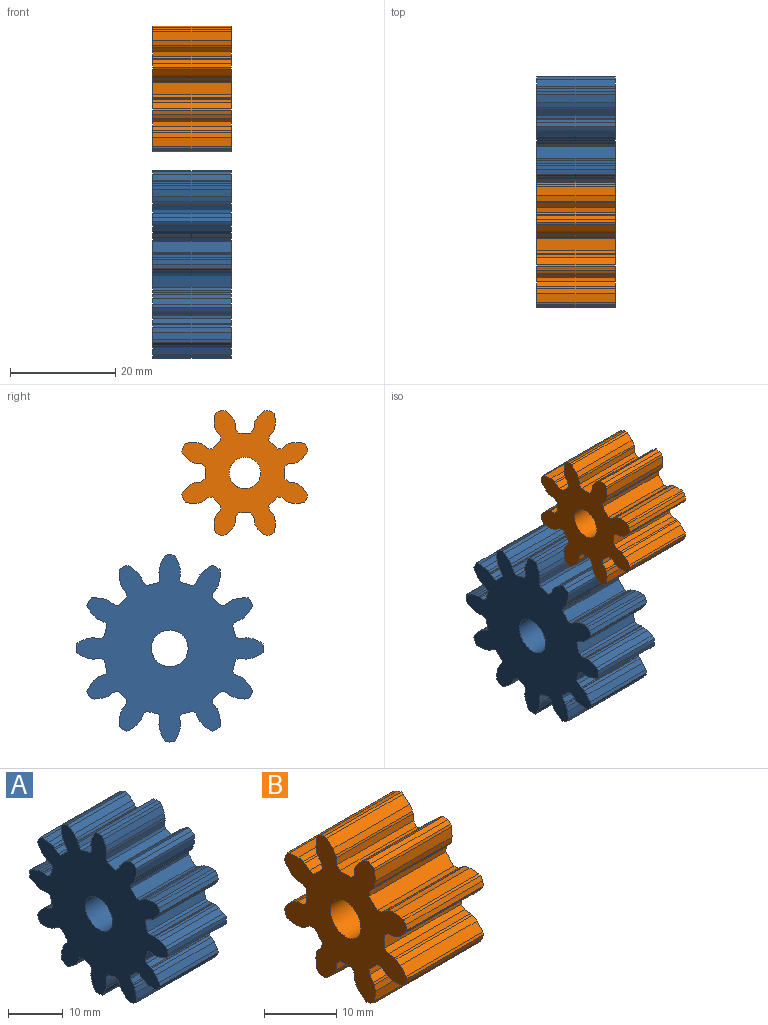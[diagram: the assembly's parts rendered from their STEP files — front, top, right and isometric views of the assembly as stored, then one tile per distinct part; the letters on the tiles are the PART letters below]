
ASSEMBLY  parts=2 mates=1
PART A: 231 faces, bbox 15x35.7x35.7 mm
  f0: plane 15x1.4mm, normal (0,-0.11,-0.99), area 21.2mm2, adj f1,f227,f228,f229
  f1: plane 15x0.66mm, normal (0,0.07,-1), area 10mm2, adj f0,f2,f228,f229
  f2: plane 15x0.69mm, normal (0,0.82,-0.57), area 12.7mm2, adj f1,f3,f228,f229
  f3: plane 15x0.77mm, normal (0,0.91,-0.42), area 12.7mm2, adj f2,f4,f228,f229
  f4: plane 15x0.6mm, normal (0,0.9,0.44), area 10mm2, adj f3,f5,f228,f229
  f5: plane 15x1.14mm, normal (0,0.81,0.59), area 21.2mm2, adj f4,f6,f228,f229
  f6: plane 15x0.7mm, normal (0,0.69,0.72), area 14.6mm2, adj f5,f7,f228,f229
  f7: plane 15x0.44mm, normal (0,0.56,0.83), area 7.9mm2, adj f6,f8,f228,f229
  f8: plane 15x0.08mm, normal (0,0.4,0.91), area 1.3mm2, adj f7,f9,f228,f229
  f9: plane 15x0.25mm, normal (0,0.24,0.97), area 3.9mm2, adj f8,f10,f228,f229
  f10: plane 15x0.9mm, normal (0,0.45,0.9), area 15mm2, adj f9,f11,f228,f229
  f11: plane 15x0.51mm, normal (0,0.83,0.56), area 9.3mm2, adj f10,f12,f228,f229
  f12: plane 15x2.2mm, normal (0,0.97,-0.26), area 34.2mm2, adj f11,f13,f228,f229
  f13: plane 15x0.56mm, normal (0,0.44,-0.9), area 9.3mm2, adj f12,f14,f228,f229
  f14: plane 15x1mm, normal (0,-0.06,-1), area 15mm2, adj f13,f15,f228,f229
  f15: plane 15x0.25mm, normal (0,-0.28,-0.96), area 3.9mm2, adj f14,f16,f228,f229
  f16: plane 15x0.09mm, normal (0,-0.11,-0.99), area 1.3mm2, adj f15,f17,f228,f229
  f17: plane 15x0.53mm, normal (0,0.07,-1), area 7.9mm2, adj f16,f18,f228,f229
  f18: plane 15x0.94mm, normal (0,0.24,-0.97), area 14.6mm2, adj f17,f19,f228,f229
  f19: plane 15x1.29mm, normal (0,0.4,-0.91), area 21.2mm2, adj f18,f20,f228,f229
  f20: plane 15x0.55mm, normal (0,0.56,-0.83), area 10mm2, adj f19,f21,f228,f229
  f21: plane 15x0.84mm, normal (0,1,-0.09), area 12.7mm2, adj f20,f22,f228,f229
  f22: plane 15x0.84mm, normal (0,1,0.09), area 12.7mm2, adj f21,f23,f228,f229
  f23: plane 15x0.55mm, normal (0,0.56,0.83), area 10mm2, adj f22,f24,f228,f229
  f24: plane 15x1.29mm, normal (0,0.4,0.91), area 21.2mm2, adj f23,f25,f228,f229
  f25: plane 15x0.94mm, normal (0,0.24,0.97), area 14.6mm2, adj f24,f26,f228,f229
  f26: plane 15x0.53mm, normal (0,0.07,1), area 7.9mm2, adj f25,f27,f228,f229
  f27: plane 15x0.09mm, normal (0,-0.11,0.99), area 1.3mm2, adj f26,f28,f228,f229
  f28: plane 15x0.25mm, normal (0,-0.28,0.96), area 3.9mm2, adj f27,f29,f228,f229
  f29: plane 15x1mm, normal (0,-0.06,1), area 15mm2, adj f28,f30,f228,f229
  f30: plane 15x0.56mm, normal (0,0.44,0.9), area 9.3mm2, adj f29,f31,f228,f229
  f31: plane 15x2.2mm, normal (0,0.97,0.26), area 34.2mm2, adj f30,f32,f228,f229
  f32: plane 15x0.51mm, normal (0,0.83,-0.56), area 9.3mm2, adj f31,f33,f228,f229
  f33: plane 15x0.9mm, normal (0,0.45,-0.9), area 15mm2, adj f32,f34,f228,f229
  f34: plane 15x0.25mm, normal (0,0.24,-0.97), area 3.9mm2, adj f33,f35,f228,f229
  f35: plane 15x0.08mm, normal (0,0.4,-0.91), area 1.3mm2, adj f34,f36,f228,f229
  f36: plane 15x0.44mm, normal (0,0.56,-0.83), area 7.9mm2, adj f35,f37,f228,f229
  f37: plane 15x0.7mm, normal (0,0.69,-0.72), area 14.6mm2, adj f36,f38,f228,f229
  f38: plane 15x1.14mm, normal (0,0.81,-0.59), area 21.2mm2, adj f37,f39,f228,f229
  f39: plane 15x0.6mm, normal (0,0.9,-0.44), area 10mm2, adj f38,f40,f228,f229
  f40: plane 15x0.77mm, normal (0,0.91,0.42), area 12.7mm2, adj f39,f41,f228,f229
  f41: plane 15x0.69mm, normal (0,0.82,0.57), area 12.7mm2, adj f40,f42,f228,f229
  f42: plane 15x0.66mm, normal (0,0.07,1), area 10mm2, adj f41,f43,f228,f229
  f43: plane 15x1.4mm, normal (0,-0.11,0.99), area 21.2mm2, adj f42,f44,f228,f229
  f44: plane 15x0.93mm, normal (0,-0.28,0.96), area 14.6mm2, adj f43,f45,f228,f229
  f45: plane 15x0.48mm, normal (0,-0.44,0.9), area 7.9mm2, adj f44,f46,f228,f229
  f46: plane 15x0.07mm, normal (0,-0.59,0.81), area 1.3mm2, adj f45,f47,f228,f229
  f47: plane 15x0.19mm, normal (0,-0.72,0.69), area 3.9mm2, adj f46,f48,f228,f229
  f48: plane 15x0.83mm, normal (0,-0.55,0.83), area 15mm2, adj f47,f49,f228,f229
  f49: plane 15x0.62mm, normal (0,-0.07,1), area 9.3mm2, adj f48,f50,f228,f229
  f50: plane 15x1.61mm, normal (0,0.71,0.71), area 34.2mm2, adj f49,f51,f228,f229
  f51: plane 15x0.62mm, normal (0,1,-0.07), area 9.3mm2, adj f50,f52,f228,f229
  f52: plane 15x0.83mm, normal (0,0.83,-0.55), area 15mm2, adj f51,f53,f228,f229
  f53: plane 15x0.19mm, normal (0,0.69,-0.72), area 3.9mm2, adj f52,f54,f228,f229
  f54: plane 15x0.07mm, normal (0,0.81,-0.59), area 1.3mm2, adj f53,f55,f228,f229
  f55: plane 15x0.48mm, normal (0,0.9,-0.44), area 7.9mm2, adj f54,f56,f228,f229
  f56: plane 15x0.93mm, normal (0,0.96,-0.28), area 14.6mm2, adj f55,f57,f228,f229
  f57: plane 15x1.4mm, normal (0,0.99,-0.11), area 21.2mm2, adj f56,f58,f228,f229
  f58: plane 15x0.66mm, normal (0,1,0.07), area 10mm2, adj f57,f59,f228,f229
  f59: plane 15x0.69mm, normal (0,0.57,0.82), area 12.7mm2, adj f58,f60,f228,f229
  f60: plane 15x0.77mm, normal (0,0.42,0.91), area 12.7mm2, adj f59,f61,f228,f229
  f61: plane 15x0.6mm, normal (0,-0.44,0.9), area 10mm2, adj f60,f62,f228,f229
  f62: plane 15x1.14mm, normal (0,-0.59,0.81), area 21.2mm2, adj f61,f63,f228,f229
  f63: plane 15x0.7mm, normal (0,-0.72,0.69), area 14.6mm2, adj f62,f64,f228,f229
  f64: plane 15x0.44mm, normal (0,-0.83,0.56), area 7.9mm2, adj f63,f65,f228,f229
  f65: plane 15x0.08mm, normal (0,-0.91,0.4), area 1.3mm2, adj f64,f66,f228,f229
  f66: plane 15x0.25mm, normal (0,-0.97,0.24), area 3.9mm2, adj f65,f67,f228,f229
  f67: plane 15x0.9mm, normal (0,-0.9,0.45), area 15mm2, adj f66,f68,f228,f229
  f68: plane 15x0.51mm, normal (0,-0.56,0.83), area 9.3mm2, adj f67,f69,f228,f229
  f69: plane 15x2.2mm, normal (0,0.26,0.97), area 34.2mm2, adj f68,f70,f228,f229
  f70: plane 15x0.56mm, normal (0,0.9,0.44), area 9.3mm2, adj f69,f71,f228,f229
  f71: plane 15x1mm, normal (0,1,-0.06), area 15mm2, adj f70,f72,f228,f229
  f72: plane 15x0.25mm, normal (0,0.96,-0.28), area 3.9mm2, adj f71,f73,f228,f229
  f73: plane 15x0.09mm, normal (0,0.99,-0.11), area 1.3mm2, adj f72,f74,f228,f229
  f74: plane 15x0.53mm, normal (0,1,0.07), area 7.9mm2, adj f73,f75,f228,f229
  f75: plane 15x0.94mm, normal (0,0.97,0.24), area 14.6mm2, adj f74,f76,f228,f229
  f76: plane 15x1.29mm, normal (0,0.91,0.4), area 21.2mm2, adj f75,f77,f228,f229
  f77: plane 15x0.55mm, normal (0,0.83,0.56), area 10mm2, adj f76,f78,f228,f229
  f78: plane 15x0.84mm, normal (0,0.09,1), area 12.7mm2, adj f77,f79,f228,f229
  f79: plane 15x0.84mm, normal (0,-0.09,1), area 12.7mm2, adj f78,f80,f228,f229
  f80: plane 15x0.55mm, normal (0,-0.83,0.56), area 10mm2, adj f79,f81,f228,f229
  f81: plane 15x1.29mm, normal (0,-0.91,0.4), area 21.2mm2, adj f80,f82,f228,f229
  f82: plane 15x0.94mm, normal (0,-0.97,0.24), area 14.6mm2, adj f81,f83,f228,f229
  f83: plane 15x0.53mm, normal (0,-1,0.07), area 7.9mm2, adj f82,f84,f228,f229
  f84: plane 15x0.09mm, normal (0,-0.99,-0.11), area 1.3mm2, adj f83,f85,f228,f229
  f85: plane 15x0.25mm, normal (0,-0.96,-0.28), area 3.9mm2, adj f84,f86,f228,f229
  f86: plane 15x1mm, normal (0,-1,-0.06), area 15mm2, adj f85,f87,f228,f229
  f87: plane 15x0.56mm, normal (0,-0.9,0.44), area 9.3mm2, adj f86,f88,f228,f229
  f88: plane 15x2.2mm, normal (0,-0.26,0.97), area 34.2mm2, adj f87,f89,f228,f229
  f89: plane 15x0.51mm, normal (0,0.56,0.83), area 9.3mm2, adj f88,f90,f228,f229
  f90: plane 15x0.9mm, normal (0,0.9,0.45), area 15mm2, adj f89,f91,f228,f229
  f91: plane 15x0.25mm, normal (0,0.97,0.24), area 3.9mm2, adj f90,f92,f228,f229
  f92: plane 15x0.08mm, normal (0,0.91,0.4), area 1.3mm2, adj f91,f93,f228,f229
  f93: plane 15x0.44mm, normal (0,0.83,0.56), area 7.9mm2, adj f92,f94,f228,f229
  f94: plane 15x0.7mm, normal (0,0.72,0.69), area 14.6mm2, adj f93,f95,f228,f229
  f95: plane 15x1.14mm, normal (0,0.59,0.81), area 21.2mm2, adj f94,f96,f228,f229
  f96: plane 15x0.6mm, normal (0,0.44,0.9), area 10mm2, adj f95,f97,f228,f229
  f97: plane 15x0.77mm, normal (0,-0.42,0.91), area 12.7mm2, adj f96,f98,f228,f229
  f98: plane 15x0.69mm, normal (0,-0.57,0.82), area 12.7mm2, adj f97,f99,f228,f229
  f99: plane 15x0.66mm, normal (0,-1,0.07), area 10mm2, adj f98,f100,f228,f229
  f100: plane 15x1.4mm, normal (0,-0.99,-0.11), area 21.2mm2, adj f99,f101,f228,f229
  f101: plane 15x0.93mm, normal (0,-0.96,-0.28), area 14.6mm2, adj f100,f102,f228,f229
  f102: plane 15x0.48mm, normal (0,-0.9,-0.44), area 7.9mm2, adj f101,f103,f228,f229
  f103: plane 15x0.07mm, normal (0,-0.81,-0.59), area 1.3mm2, adj f102,f104,f228,f229
  f104: plane 15x0.19mm, normal (0,-0.69,-0.72), area 3.9mm2, adj f103,f105,f228,f229
  f105: plane 15x0.83mm, normal (0,-0.83,-0.55), area 15mm2, adj f104,f106,f228,f229
  f106: plane 15x0.62mm, normal (0,-1,-0.07), area 9.3mm2, adj f105,f107,f228,f229
  f107: plane 15x1.61mm, normal (0,-0.71,0.71), area 34.2mm2, adj f106,f108,f228,f229
  f108: plane 15x0.62mm, normal (0,0.07,1), area 9.3mm2, adj f107,f109,f228,f229
  f109: plane 15x0.83mm, normal (0,0.55,0.83), area 15mm2, adj f108,f110,f228,f229
  f110: plane 15x0.19mm, normal (0,0.72,0.69), area 3.9mm2, adj f109,f111,f228,f229
  f111: plane 15x0.07mm, normal (0,0.59,0.81), area 1.3mm2, adj f110,f112,f228,f229
  f112: plane 15x0.48mm, normal (0,0.44,0.9), area 7.9mm2, adj f111,f113,f228,f229
  f113: plane 15x0.93mm, normal (0,0.28,0.96), area 14.6mm2, adj f112,f114,f228,f229
  f114: plane 15x1.4mm, normal (0,0.11,0.99), area 21.2mm2, adj f113,f115,f228,f229
  f115: plane 15x0.66mm, normal (0,-0.07,1), area 10mm2, adj f114,f116,f228,f229
  f116: plane 15x0.69mm, normal (0,-0.82,0.57), area 12.7mm2, adj f115,f117,f228,f229
  f117: plane 15x0.77mm, normal (0,-0.91,0.42), area 12.7mm2, adj f116,f118,f228,f229
  f118: plane 15x0.6mm, normal (0,-0.9,-0.44), area 10mm2, adj f117,f119,f228,f229
  f119: plane 15x1.14mm, normal (0,-0.81,-0.59), area 21.2mm2, adj f118,f120,f228,f229
  f120: plane 15x0.7mm, normal (0,-0.69,-0.72), area 14.6mm2, adj f119,f121,f228,f229
  f121: plane 15x0.44mm, normal (0,-0.56,-0.83), area 7.9mm2, adj f120,f122,f228,f229
  f122: plane 15x0.08mm, normal (0,-0.4,-0.91), area 1.3mm2, adj f121,f123,f228,f229
  f123: plane 15x0.25mm, normal (0,-0.24,-0.97), area 3.9mm2, adj f122,f124,f228,f229
  f124: plane 15x0.9mm, normal (0,-0.45,-0.9), area 15mm2, adj f123,f125,f228,f229
  f125: plane 15x0.51mm, normal (0,-0.83,-0.56), area 9.3mm2, adj f124,f126,f228,f229
  f126: plane 15x2.2mm, normal (0,-0.97,0.26), area 34.2mm2, adj f125,f127,f228,f229
  f127: plane 15x0.56mm, normal (0,-0.44,0.9), area 9.3mm2, adj f126,f128,f228,f229
  f128: plane 15x1mm, normal (0,0.06,1), area 15mm2, adj f127,f129,f228,f229
  f129: plane 15x0.25mm, normal (0,0.28,0.96), area 3.9mm2, adj f128,f130,f228,f229
  f130: plane 15x0.09mm, normal (0,0.11,0.99), area 1.3mm2, adj f129,f131,f228,f229
  f131: plane 15x0.53mm, normal (0,-0.07,1), area 7.9mm2, adj f130,f132,f228,f229
  f132: plane 15x0.94mm, normal (0,-0.24,0.97), area 14.6mm2, adj f131,f133,f228,f229
  f133: plane 15x1.29mm, normal (0,-0.4,0.91), area 21.2mm2, adj f132,f134,f228,f229
  f134: plane 15x0.55mm, normal (0,-0.56,0.83), area 10mm2, adj f133,f135,f228,f229
  f135: plane 15x0.84mm, normal (0,-1,0.09), area 12.7mm2, adj f134,f136,f228,f229
  f136: plane 15x0.84mm, normal (0,-1,-0.09), area 12.7mm2, adj f135,f137,f228,f229
  f137: plane 15x0.55mm, normal (0,-0.56,-0.83), area 10mm2, adj f136,f138,f228,f229
  f138: plane 15x1.29mm, normal (0,-0.4,-0.91), area 21.2mm2, adj f137,f139,f228,f229
  f139: plane 15x0.94mm, normal (0,-0.24,-0.97), area 14.6mm2, adj f138,f140,f228,f229
  f140: plane 15x0.53mm, normal (0,-0.07,-1), area 7.9mm2, adj f139,f141,f228,f229
  f141: plane 15x0.09mm, normal (0,0.11,-0.99), area 1.3mm2, adj f140,f142,f228,f229
  f142: plane 15x0.25mm, normal (0,0.28,-0.96), area 3.9mm2, adj f141,f143,f228,f229
  f143: plane 15x1mm, normal (0,0.06,-1), area 15mm2, adj f142,f144,f228,f229
  f144: plane 15x0.56mm, normal (0,-0.44,-0.9), area 9.3mm2, adj f143,f145,f228,f229
  f145: plane 15x2.2mm, normal (0,-0.97,-0.26), area 34.2mm2, adj f144,f146,f228,f229
  f146: plane 15x0.51mm, normal (0,-0.83,0.56), area 9.3mm2, adj f145,f147,f228,f229
  f147: plane 15x0.9mm, normal (0,-0.45,0.9), area 15mm2, adj f146,f148,f228,f229
  f148: plane 15x0.25mm, normal (0,-0.24,0.97), area 3.9mm2, adj f147,f149,f228,f229
  f149: plane 15x0.08mm, normal (0,-0.4,0.91), area 1.3mm2, adj f148,f150,f228,f229
  f150: plane 15x0.44mm, normal (0,-0.56,0.83), area 7.9mm2, adj f149,f151,f228,f229
  f151: plane 15x0.7mm, normal (0,-0.69,0.72), area 14.6mm2, adj f150,f152,f228,f229
  f152: plane 15x1.14mm, normal (0,-0.81,0.59), area 21.2mm2, adj f151,f153,f228,f229
  f153: plane 15x0.6mm, normal (0,-0.9,0.44), area 10mm2, adj f152,f154,f228,f229
  f154: plane 15x0.77mm, normal (0,-0.91,-0.42), area 12.7mm2, adj f153,f155,f228,f229
  f155: plane 15x0.69mm, normal (0,-0.82,-0.57), area 12.7mm2, adj f154,f156,f228,f229
  f156: plane 15x0.66mm, normal (0,-0.07,-1), area 10mm2, adj f155,f157,f228,f229
  f157: plane 15x1.4mm, normal (0,0.11,-0.99), area 21.2mm2, adj f156,f158,f228,f229
  f158: plane 15x0.93mm, normal (0,0.28,-0.96), area 14.6mm2, adj f157,f159,f228,f229
  f159: plane 15x0.48mm, normal (0,0.44,-0.9), area 7.9mm2, adj f158,f160,f228,f229
  f160: plane 15x0.07mm, normal (0,0.59,-0.81), area 1.3mm2, adj f159,f161,f228,f229
  f161: plane 15x0.19mm, normal (0,0.72,-0.69), area 3.9mm2, adj f160,f162,f228,f229
  f162: plane 15x0.83mm, normal (0,0.55,-0.83), area 15mm2, adj f161,f163,f228,f229
  f163: plane 15x0.62mm, normal (0,0.07,-1), area 9.3mm2, adj f162,f164,f228,f229
  f164: plane 15x1.61mm, normal (0,-0.71,-0.71), area 34.2mm2, adj f163,f165,f228,f229
  f165: plane 15x0.62mm, normal (0,-1,0.07), area 9.3mm2, adj f164,f166,f228,f229
  f166: plane 15x0.83mm, normal (0,-0.83,0.55), area 15mm2, adj f165,f167,f228,f229
  f167: plane 15x0.19mm, normal (0,-0.69,0.72), area 3.9mm2, adj f166,f168,f228,f229
  f168: plane 15x0.07mm, normal (0,-0.81,0.59), area 1.3mm2, adj f167,f169,f228,f229
  f169: plane 15x0.48mm, normal (0,-0.9,0.44), area 7.9mm2, adj f168,f170,f228,f229
  f170: plane 15x0.93mm, normal (0,-0.96,0.28), area 14.6mm2, adj f169,f171,f228,f229
  f171: plane 15x1.4mm, normal (0,-0.99,0.11), area 21.2mm2, adj f170,f172,f228,f229
  f172: plane 15x0.66mm, normal (0,-1,-0.07), area 10mm2, adj f171,f173,f228,f229
  f173: plane 15x0.69mm, normal (0,-0.57,-0.82), area 12.7mm2, adj f172,f174,f228,f229
  f174: plane 15x0.77mm, normal (0,-0.42,-0.91), area 12.7mm2, adj f173,f175,f228,f229
  f175: plane 15x0.6mm, normal (0,0.44,-0.9), area 10mm2, adj f174,f176,f228,f229
  f176: plane 15x1.14mm, normal (0,0.59,-0.81), area 21.2mm2, adj f175,f177,f228,f229
  f177: plane 15x0.7mm, normal (0,0.72,-0.69), area 14.6mm2, adj f176,f178,f228,f229
  f178: plane 15x0.44mm, normal (0,0.83,-0.56), area 7.9mm2, adj f177,f179,f228,f229
  f179: plane 15x0.08mm, normal (0,0.91,-0.4), area 1.3mm2, adj f178,f180,f228,f229
  f180: plane 15x0.25mm, normal (0,0.97,-0.24), area 3.9mm2, adj f179,f181,f228,f229
  f181: plane 15x0.9mm, normal (0,0.9,-0.45), area 15mm2, adj f180,f182,f228,f229
  f182: plane 15x0.51mm, normal (0,0.56,-0.83), area 9.3mm2, adj f181,f183,f228,f229
  f183: plane 15x2.2mm, normal (0,-0.26,-0.97), area 34.2mm2, adj f182,f184,f228,f229
  f184: plane 15x0.56mm, normal (0,-0.9,-0.44), area 9.3mm2, adj f183,f185,f228,f229
  f185: plane 15x1mm, normal (0,-1,0.06), area 15mm2, adj f184,f186,f228,f229
  f186: plane 15x0.25mm, normal (0,-0.96,0.28), area 3.9mm2, adj f185,f187,f228,f229
  f187: plane 15x0.09mm, normal (0,-0.99,0.11), area 1.3mm2, adj f186,f188,f228,f229
  f188: plane 15x0.53mm, normal (0,-1,-0.07), area 7.9mm2, adj f187,f189,f228,f229
  f189: plane 15x0.94mm, normal (0,-0.97,-0.24), area 14.6mm2, adj f188,f190,f228,f229
  f190: plane 15x1.29mm, normal (0,-0.91,-0.4), area 21.2mm2, adj f189,f191,f228,f229
  f191: plane 15x0.55mm, normal (0,-0.83,-0.56), area 10mm2, adj f190,f192,f228,f229
  f192: plane 15x0.84mm, normal (0,-0.09,-1), area 12.7mm2, adj f191,f193,f228,f229
  f193: plane 15x0.84mm, normal (0,0.09,-1), area 12.7mm2, adj f192,f194,f228,f229
  f194: plane 15x0.55mm, normal (0,0.83,-0.56), area 10mm2, adj f193,f195,f228,f229
  f195: plane 15x1.29mm, normal (0,0.91,-0.4), area 21.2mm2, adj f194,f196,f228,f229
  f196: plane 15x0.94mm, normal (0,0.97,-0.24), area 14.6mm2, adj f195,f197,f228,f229
  f197: plane 15x0.53mm, normal (0,1,-0.07), area 7.9mm2, adj f196,f198,f228,f229
  f198: plane 15x0.09mm, normal (0,0.99,0.11), area 1.3mm2, adj f197,f199,f228,f229
  f199: plane 15x0.25mm, normal (0,0.96,0.28), area 3.9mm2, adj f198,f200,f228,f229
  f200: plane 15x1mm, normal (0,1,0.06), area 15mm2, adj f199,f201,f228,f229
  f201: plane 15x0.56mm, normal (0,0.9,-0.44), area 9.3mm2, adj f200,f202,f228,f229
  f202: plane 15x2.2mm, normal (0,0.26,-0.97), area 34.2mm2, adj f201,f203,f228,f229
  f203: plane 15x0.51mm, normal (0,-0.56,-0.83), area 9.3mm2, adj f202,f204,f228,f229
  f204: plane 15x0.9mm, normal (0,-0.9,-0.45), area 15mm2, adj f203,f205,f228,f229
  f205: plane 15x0.25mm, normal (0,-0.97,-0.24), area 3.9mm2, adj f204,f206,f228,f229
  f206: plane 15x0.08mm, normal (0,-0.91,-0.4), area 1.3mm2, adj f205,f207,f228,f229
  f207: plane 15x0.44mm, normal (0,-0.83,-0.56), area 7.9mm2, adj f206,f208,f228,f229
  f208: plane 15x0.7mm, normal (0,-0.72,-0.69), area 14.6mm2, adj f207,f209,f228,f229
  f209: plane 15x1.14mm, normal (0,-0.59,-0.81), area 21.2mm2, adj f208,f210,f228,f229
  f210: plane 15x0.6mm, normal (0,-0.44,-0.9), area 10mm2, adj f209,f211,f228,f229
  f211: plane 15x0.77mm, normal (0,0.42,-0.91), area 12.7mm2, adj f210,f212,f228,f229
  f212: plane 15x0.69mm, normal (0,0.57,-0.82), area 12.7mm2, adj f211,f213,f228,f229
  f213: plane 15x0.66mm, normal (0,1,-0.07), area 10mm2, adj f212,f214,f228,f229
  f214: plane 15x1.4mm, normal (0,0.99,0.11), area 21.2mm2, adj f213,f215,f228,f229
  f215: plane 15x0.93mm, normal (0,0.96,0.28), area 14.6mm2, adj f214,f216,f228,f229
  f216: plane 15x0.48mm, normal (0,0.9,0.44), area 7.9mm2, adj f215,f217,f228,f229
  f217: plane 15x0.07mm, normal (0,0.81,0.59), area 1.3mm2, adj f216,f218,f228,f229
  f218: plane 15x0.19mm, normal (0,0.69,0.72), area 3.9mm2, adj f217,f219,f228,f229
  f219: plane 15x0.83mm, normal (0,0.83,0.55), area 15mm2, adj f218,f220,f228,f229
  f220: plane 15x0.62mm, normal (0,1,0.07), area 9.3mm2, adj f219,f221,f228,f229
  f221: plane 15x1.61mm, normal (0,0.71,-0.71), area 34.2mm2, adj f220,f222,f228,f229
  f222: plane 15x0.62mm, normal (0,-0.07,-1), area 9.3mm2, adj f221,f223,f228,f229
  f223: plane 15x0.83mm, normal (0,-0.55,-0.83), area 15mm2, adj f222,f224,f228,f229
  f224: plane 15x0.19mm, normal (0,-0.72,-0.69), area 3.9mm2, adj f223,f225,f228,f229
  f225: plane 15x0.07mm, normal (0,-0.59,-0.81), area 1.3mm2, adj f224,f226,f228,f229
  f226: plane 15x0.48mm, normal (0,-0.44,-0.9), area 7.9mm2, adj f225,f227,f228,f229
  f227: plane 15x0.93mm, normal (0,-0.28,-0.96), area 14.6mm2, adj f0,f226,f228,f229
  f228: plane 35.65x35.65mm, normal (1,0,0), area 683.3mm2, adj f0,f1,f2,f3,f4,f5,f6,f7
  f229: plane 35.65x35.65mm, normal (-1,0,0), area 683.3mm2, adj f0,f1,f2,f3,f4,f5,f6,f7
  f230: cylinder r=3.5mm len=15mm, axis (-1,0,0), area 329.9mm2, adj f228,f229
PART B: 123 faces, bbox 15x24x24 mm
  f0: plane 15x1.69mm, normal (0,-0.07,1), area 25.4mm2, adj f1,f119,f120,f121
  f1: plane 15x0.39mm, normal (0,-0.32,0.95), area 6.2mm2, adj f0,f2,f120,f121
  f2: plane 15x0.69mm, normal (0,-0.88,0.47), area 11.7mm2, adj f1,f3,f120,f121
  f3: plane 15x0.75mm, normal (0,-0.96,0.29), area 11.7mm2, adj f2,f4,f120,f121
  f4: plane 15x0.37mm, normal (0,-0.9,-0.44), area 6.2mm2, adj f3,f5,f120,f121
  f5: plane 15x1.27mm, normal (0,-0.75,-0.66), area 25.4mm2, adj f4,f6,f120,f121
  f6: plane 15x0.85mm, normal (0,-0.56,-0.83), area 15.4mm2, adj f5,f7,f120,f121
  f7: plane 15x0.34mm, normal (0,-0.32,-0.95), area 5.4mm2, adj f6,f8,f120,f121
  f8: plane 15x1.18mm, normal (0,-0.07,-1), area 17.8mm2, adj f7,f9,f120,f121
  f9: plane 15x0.73mm, normal (0,-0.62,-0.79), area 13.9mm2, adj f8,f10,f120,f121
  f10: plane 15x2.28mm, normal (0,-1,0), area 34.2mm2, adj f9,f11,f120,f121
  f11: plane 15x0.73mm, normal (0,-0.62,0.79), area 13.9mm2, adj f10,f12,f120,f121
  f12: plane 15x1.18mm, normal (0,-0.07,1), area 17.8mm2, adj f11,f13,f120,f121
  f13: plane 15x0.34mm, normal (0,-0.32,0.95), area 5.4mm2, adj f12,f14,f120,f121
  f14: plane 15x0.85mm, normal (0,-0.56,0.83), area 15.4mm2, adj f13,f15,f120,f121
  f15: plane 15x1.27mm, normal (0,-0.75,0.66), area 25.4mm2, adj f14,f16,f120,f121
  f16: plane 15x0.37mm, normal (0,-0.9,0.44), area 6.2mm2, adj f15,f17,f120,f121
  f17: plane 15x0.75mm, normal (0,-0.96,-0.29), area 11.7mm2, adj f16,f18,f120,f121
  f18: plane 15x0.69mm, normal (0,-0.88,-0.47), area 11.7mm2, adj f17,f19,f120,f121
  f19: plane 15x0.39mm, normal (0,-0.32,-0.95), area 6.2mm2, adj f18,f20,f120,f121
  f20: plane 15x1.69mm, normal (0,-0.07,-1), area 25.4mm2, adj f19,f21,f120,f121
  f21: plane 15x1.01mm, normal (0,0.19,-0.98), area 15.4mm2, adj f20,f22,f120,f121
  f22: plane 15x0.33mm, normal (0,0.44,-0.9), area 5.4mm2, adj f21,f23,f120,f121
  f23: plane 15x0.89mm, normal (0,0.66,-0.75), area 17.8mm2, adj f22,f24,f120,f121
  f24: plane 15x0.92mm, normal (0,0.12,-0.99), area 13.9mm2, adj f23,f25,f120,f121
  f25: plane 15x1.61mm, normal (0,-0.71,-0.71), area 34.2mm2, adj f24,f26,f120,f121
  f26: plane 15x0.92mm, normal (0,-0.99,0.12), area 13.9mm2, adj f25,f27,f120,f121
  f27: plane 15x0.89mm, normal (0,-0.75,0.66), area 17.8mm2, adj f26,f28,f120,f121
  f28: plane 15x0.33mm, normal (0,-0.9,0.44), area 5.4mm2, adj f27,f29,f120,f121
  f29: plane 15x1.01mm, normal (0,-0.98,0.19), area 15.4mm2, adj f28,f30,f120,f121
  f30: plane 15x1.69mm, normal (0,-1,-0.07), area 25.4mm2, adj f29,f31,f120,f121
  f31: plane 15x0.39mm, normal (0,-0.95,-0.32), area 6.2mm2, adj f30,f32,f120,f121
  f32: plane 15x0.69mm, normal (0,-0.47,-0.88), area 11.7mm2, adj f31,f33,f120,f121
  f33: plane 15x0.75mm, normal (0,-0.29,-0.96), area 11.7mm2, adj f32,f34,f120,f121
  f34: plane 15x0.37mm, normal (0,0.44,-0.9), area 6.2mm2, adj f33,f35,f120,f121
  f35: plane 15x1.27mm, normal (0,0.66,-0.75), area 25.4mm2, adj f34,f36,f120,f121
  f36: plane 15x0.85mm, normal (0,0.83,-0.56), area 15.4mm2, adj f35,f37,f120,f121
  f37: plane 15x0.34mm, normal (0,0.95,-0.32), area 5.4mm2, adj f36,f38,f120,f121
  f38: plane 15x1.18mm, normal (0,1,-0.07), area 17.8mm2, adj f37,f39,f120,f121
  f39: plane 15x0.73mm, normal (0,0.79,-0.62), area 13.9mm2, adj f38,f40,f120,f121
  f40: plane 15x2.28mm, normal (0,0,-1), area 34.2mm2, adj f39,f41,f120,f121
  f41: plane 15x0.73mm, normal (0,-0.79,-0.62), area 13.9mm2, adj f40,f42,f120,f121
  f42: plane 15x1.18mm, normal (0,-1,-0.07), area 17.8mm2, adj f41,f43,f120,f121
  f43: plane 15x0.34mm, normal (0,-0.95,-0.32), area 5.4mm2, adj f42,f44,f120,f121
  f44: plane 15x0.85mm, normal (0,-0.83,-0.56), area 15.4mm2, adj f43,f45,f120,f121
  f45: plane 15x1.27mm, normal (0,-0.66,-0.75), area 25.4mm2, adj f44,f46,f120,f121
  f46: plane 15x0.37mm, normal (0,-0.44,-0.9), area 6.2mm2, adj f45,f47,f120,f121
  f47: plane 15x0.75mm, normal (0,0.29,-0.96), area 11.7mm2, adj f46,f48,f120,f121
  f48: plane 15x0.69mm, normal (0,0.47,-0.88), area 11.7mm2, adj f47,f49,f120,f121
  f49: plane 15x0.39mm, normal (0,0.95,-0.32), area 6.2mm2, adj f48,f50,f120,f121
  f50: plane 15x1.69mm, normal (0,1,-0.07), area 25.4mm2, adj f49,f51,f120,f121
  f51: plane 15x1.01mm, normal (0,0.98,0.19), area 15.4mm2, adj f50,f52,f120,f121
  f52: plane 15x0.33mm, normal (0,0.9,0.44), area 5.4mm2, adj f51,f53,f120,f121
  f53: plane 15x0.89mm, normal (0,0.75,0.66), area 17.8mm2, adj f52,f54,f120,f121
  f54: plane 15x0.92mm, normal (0,0.99,0.12), area 13.9mm2, adj f53,f55,f120,f121
  f55: plane 15x1.61mm, normal (0,0.71,-0.71), area 34.2mm2, adj f54,f56,f120,f121
  f56: plane 15x0.92mm, normal (0,-0.12,-0.99), area 13.9mm2, adj f55,f57,f120,f121
  f57: plane 15x0.89mm, normal (0,-0.66,-0.75), area 17.8mm2, adj f56,f58,f120,f121
  f58: plane 15x0.33mm, normal (0,-0.44,-0.9), area 5.4mm2, adj f57,f59,f120,f121
  f59: plane 15x1.01mm, normal (0,-0.19,-0.98), area 15.4mm2, adj f58,f60,f120,f121
  f60: plane 15x1.69mm, normal (0,0.07,-1), area 25.4mm2, adj f59,f61,f120,f121
  f61: plane 15x0.39mm, normal (0,0.32,-0.95), area 6.2mm2, adj f60,f62,f120,f121
  f62: plane 15x0.69mm, normal (0,0.88,-0.47), area 11.7mm2, adj f61,f63,f120,f121
  f63: plane 15x0.75mm, normal (0,0.96,-0.29), area 11.7mm2, adj f62,f64,f120,f121
  f64: plane 15x0.37mm, normal (0,0.9,0.44), area 6.2mm2, adj f63,f65,f120,f121
  f65: plane 15x1.27mm, normal (0,0.75,0.66), area 25.4mm2, adj f64,f66,f120,f121
  f66: plane 15x0.85mm, normal (0,0.56,0.83), area 15.4mm2, adj f65,f67,f120,f121
  f67: plane 15x0.34mm, normal (0,0.32,0.95), area 5.4mm2, adj f66,f68,f120,f121
  f68: plane 15x1.18mm, normal (0,0.07,1), area 17.8mm2, adj f67,f69,f120,f121
  f69: plane 15x0.73mm, normal (0,0.62,0.79), area 13.9mm2, adj f68,f70,f120,f121
  f70: plane 15x2.28mm, normal (0,1,0), area 34.2mm2, adj f69,f71,f120,f121
  f71: plane 15x0.73mm, normal (0,0.62,-0.79), area 13.9mm2, adj f70,f72,f120,f121
  f72: plane 15x1.18mm, normal (0,0.07,-1), area 17.8mm2, adj f71,f73,f120,f121
  f73: plane 15x0.34mm, normal (0,0.32,-0.95), area 5.4mm2, adj f72,f74,f120,f121
  f74: plane 15x0.85mm, normal (0,0.56,-0.83), area 15.4mm2, adj f73,f75,f120,f121
  f75: plane 15x1.27mm, normal (0,0.75,-0.66), area 25.4mm2, adj f74,f76,f120,f121
  f76: plane 15x0.37mm, normal (0,0.9,-0.44), area 6.2mm2, adj f75,f77,f120,f121
  f77: plane 15x0.75mm, normal (0,0.96,0.29), area 11.7mm2, adj f76,f78,f120,f121
  f78: plane 15x0.69mm, normal (0,0.88,0.47), area 11.7mm2, adj f77,f79,f120,f121
  f79: plane 15x0.39mm, normal (0,0.32,0.95), area 6.2mm2, adj f78,f80,f120,f121
  f80: plane 15x1.69mm, normal (0,0.07,1), area 25.4mm2, adj f79,f81,f120,f121
  f81: plane 15x1.01mm, normal (0,-0.19,0.98), area 15.4mm2, adj f80,f82,f120,f121
  f82: plane 15x0.33mm, normal (0,-0.44,0.9), area 5.4mm2, adj f81,f83,f120,f121
  f83: plane 15x0.89mm, normal (0,-0.66,0.75), area 17.8mm2, adj f82,f84,f120,f121
  f84: plane 15x0.92mm, normal (0,-0.12,0.99), area 13.9mm2, adj f83,f85,f120,f121
  f85: plane 15x1.61mm, normal (0,0.71,0.71), area 34.2mm2, adj f84,f86,f120,f121
  f86: plane 15x0.92mm, normal (0,0.99,-0.12), area 13.9mm2, adj f85,f87,f120,f121
  f87: plane 15x0.89mm, normal (0,0.75,-0.66), area 17.8mm2, adj f86,f88,f120,f121
  f88: plane 15x0.33mm, normal (0,0.9,-0.44), area 5.4mm2, adj f87,f89,f120,f121
  f89: plane 15x1.01mm, normal (0,0.98,-0.19), area 15.4mm2, adj f88,f90,f120,f121
  f90: plane 15x1.69mm, normal (0,1,0.07), area 25.4mm2, adj f89,f91,f120,f121
  f91: plane 15x0.39mm, normal (0,0.95,0.32), area 6.2mm2, adj f90,f92,f120,f121
  f92: plane 15x0.69mm, normal (0,0.47,0.88), area 11.7mm2, adj f91,f93,f120,f121
  f93: plane 15x0.75mm, normal (0,0.29,0.96), area 11.7mm2, adj f92,f94,f120,f121
  f94: plane 15x0.37mm, normal (0,-0.44,0.9), area 6.2mm2, adj f93,f95,f120,f121
  f95: plane 15x1.27mm, normal (0,-0.66,0.75), area 25.4mm2, adj f94,f96,f120,f121
  f96: plane 15x0.85mm, normal (0,-0.83,0.56), area 15.4mm2, adj f95,f97,f120,f121
  f97: plane 15x0.34mm, normal (0,-0.95,0.32), area 5.4mm2, adj f96,f98,f120,f121
  f98: plane 15x1.18mm, normal (0,-1,0.07), area 17.8mm2, adj f97,f99,f120,f121
  f99: plane 15x0.73mm, normal (0,-0.79,0.62), area 13.9mm2, adj f98,f100,f120,f121
  f100: plane 15x2.28mm, normal (0,0,1), area 34.2mm2, adj f99,f101,f120,f121
  f101: plane 15x0.73mm, normal (0,0.79,0.62), area 13.9mm2, adj f100,f102,f120,f121
  f102: plane 15x1.18mm, normal (0,1,0.07), area 17.8mm2, adj f101,f103,f120,f121
  f103: plane 15x0.34mm, normal (0,0.95,0.32), area 5.4mm2, adj f102,f104,f120,f121
  f104: plane 15x0.85mm, normal (0,0.83,0.56), area 15.4mm2, adj f103,f105,f120,f121
  f105: plane 15x1.27mm, normal (0,0.66,0.75), area 25.4mm2, adj f104,f106,f120,f121
  f106: plane 15x0.37mm, normal (0,0.44,0.9), area 6.2mm2, adj f105,f107,f120,f121
  f107: plane 15x0.75mm, normal (0,-0.29,0.96), area 11.7mm2, adj f106,f108,f120,f121
  f108: plane 15x0.69mm, normal (0,-0.47,0.88), area 11.7mm2, adj f107,f109,f120,f121
  f109: plane 15x0.39mm, normal (0,-0.95,0.32), area 6.2mm2, adj f108,f110,f120,f121
  f110: plane 15x1.69mm, normal (0,-1,0.07), area 25.4mm2, adj f109,f111,f120,f121
  f111: plane 15x1.01mm, normal (0,-0.98,-0.19), area 15.4mm2, adj f110,f112,f120,f121
  f112: plane 15x0.33mm, normal (0,-0.9,-0.44), area 5.4mm2, adj f111,f113,f120,f121
  f113: plane 15x0.89mm, normal (0,-0.75,-0.66), area 17.8mm2, adj f112,f114,f120,f121
  f114: plane 15x0.92mm, normal (0,-0.99,-0.12), area 13.9mm2, adj f113,f115,f120,f121
  f115: plane 15x1.61mm, normal (0,-0.71,0.71), area 34.2mm2, adj f114,f116,f120,f121
  f116: plane 15x0.92mm, normal (0,0.12,0.99), area 13.9mm2, adj f115,f117,f120,f121
  f117: plane 15x0.89mm, normal (0,0.66,0.75), area 17.8mm2, adj f116,f118,f120,f121
  f118: plane 15x0.33mm, normal (0,0.44,0.9), area 5.4mm2, adj f117,f119,f120,f121
  f119: plane 15x1.01mm, normal (0,0.19,0.98), area 15.4mm2, adj f0,f118,f120,f121
  f120: plane 23.98x23.98mm, normal (1,0,0), area 289.7mm2, adj f0,f1,f2,f3,f4,f5,f6,f7
  f121: plane 23.98x23.98mm, normal (-1,0,0), area 289.7mm2, adj f0,f1,f2,f3,f4,f5,f6,f7
  f122: cylinder r=3mm len=15mm, axis (-1,0,0), area 282.7mm2, adj f120,f121
PLACE A t=(35.73,43.61,-3.86)mm
PLACE B t=(35.73,3.85,29.53)mm
MATE parallel A.f229 <-> B.f121  axis (-1,0,0) through (35.73,37.08,8.39)mm
